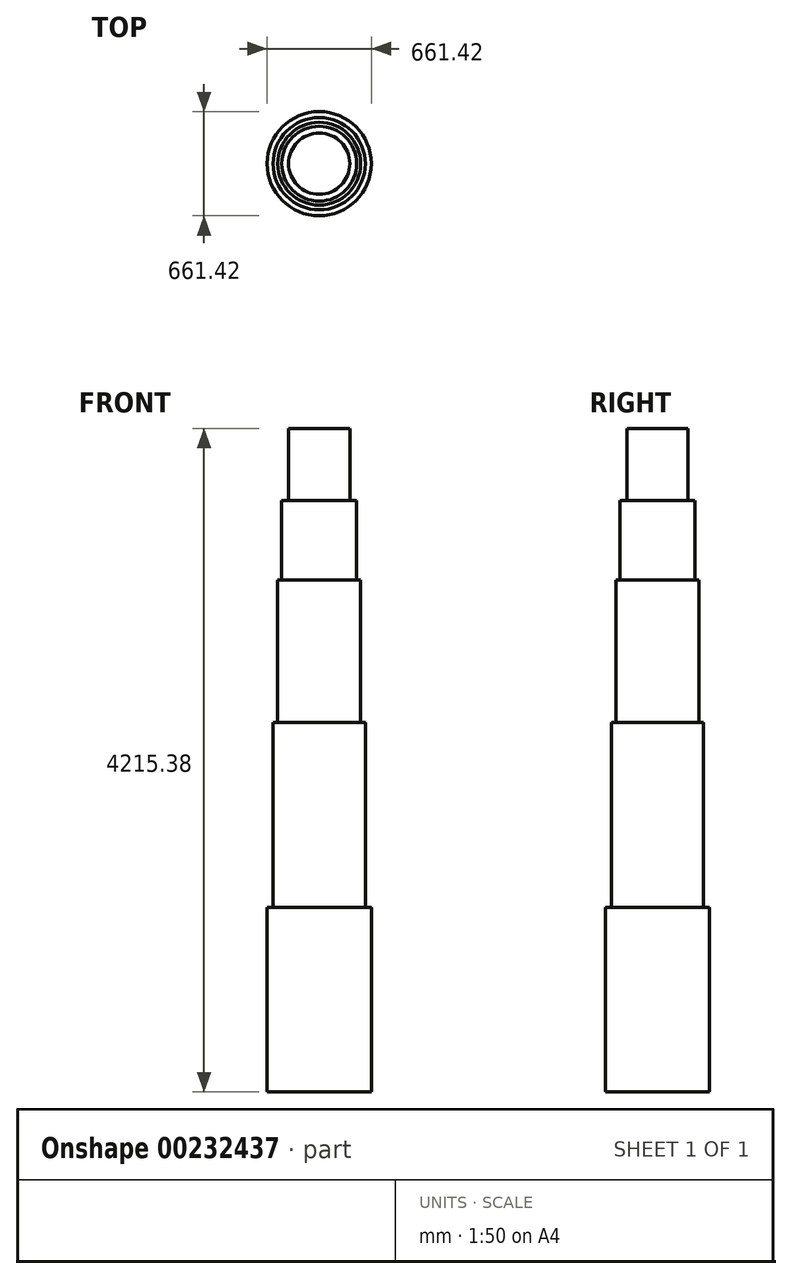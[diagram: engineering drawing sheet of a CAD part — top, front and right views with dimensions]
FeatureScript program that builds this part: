
annotation { "Feature Type Name" : "Feature", "Feature Type Description" : "" }
export const myFeature = defineFeature(function(context is Context, id is Id, definition is map)
    precondition{}
    {
        {
            var Q0;
            Q0=qCreatedBy(makeId("Top.planeOp"),FACE);
            var sketch = newSketch(context, id + "F0", { "sketchPlane" : qUnion([Q0])});
            skCircle(sketch, "E0", {"center": v(0, 0) * mm, "radius": 330.7 * mm});
            skSolve(sketch);
        }
        {
            var Q0;
            Q0 = qSketchRegion(id + "F0", true);
            extrude(context, id + "F1", {"entities" : qUnion([Q0]), "depth" : 1172.46 * mm});
        }
        {
            var Q0;
            Q0=makeQuery(id+"F1.opExtrude","CAP_FACE",FACE,{"disambiguationData":[OSD([sQuery(id+"F0.wireOp",EDGE,"E0")])],"isStart":false});
            var sketch = newSketch(context, id + "F2", { "sketchPlane" : qUnion([Q0])});
            skCircle(sketch, "E1", {"center": v(0, 0) * mm, "radius": 292.86 * mm});
            skSolve(sketch);
        }
        {
            var Q0;
            Q0 = qSketchRegion(id + "F2", true);
            extrude(context, id + "F3", {"entities" : qUnion([Q0]), "operationType" : NewBodyOperationType.ADD, "depth" : 1175 * mm});
        }
        {
            var Q0;
            Q0=makeQuery(id+"F3.opExtrude","CAP_FACE",FACE,{"disambiguationData":[OSD([sQuery(id+"F2.wireOp",EDGE,"E1")])],"isStart":false});
            var sketch = newSketch(context, id + "F4", { "sketchPlane" : qUnion([Q0])});
            skCircle(sketch, "E2", {"center": v(0, 0) * mm, "radius": 263.14 * mm});
            skSolve(sketch);
        }
        {
            var Q0;
            Q0 = qSketchRegion(id + "F4", true);
            extrude(context, id + "F5", {"entities" : qUnion([Q0]), "operationType" : NewBodyOperationType.ADD, "depth" : 905 * mm});
        }
        {
            var Q0;
            Q0=makeQuery(id+"F5.opExtrude","CAP_FACE",FACE,{"disambiguationData":[OSD([sQuery(id+"F4.wireOp",EDGE,"E2")])],"isStart":false});
            var sketch = newSketch(context, id + "F6", { "sketchPlane" : qUnion([Q0])});
            skCircle(sketch, "E3", {"center": v(0, 0) * mm, "radius": 237.74 * mm});
            skSolve(sketch);
        }
        {
            var Q0;
            Q0 = qSketchRegion(id + "F6", true);
            extrude(context, id + "F7", {"entities" : qUnion([Q0]), "operationType" : NewBodyOperationType.ADD, "depth" : 503.43 * mm});
        }
        {
            var Q0;
            Q0=makeQuery(id+"F7.opExtrude","CAP_FACE",FACE,{"disambiguationData":[OSD([sQuery(id+"F6.wireOp",EDGE,"E3")])],"isStart":false});
            var sketch = newSketch(context, id + "F8", { "sketchPlane" : qUnion([Q0])});
            skCircle(sketch, "E4", {"center": v(0, 0) * mm, "radius": 194.31 * mm});
            skSolve(sketch);
        }
        {
            var Q0;
            Q0 = qSketchRegion(id + "F8", true);
            extrude(context, id + "F9", {"entities" : qUnion([Q0]), "operationType" : NewBodyOperationType.ADD, "depth" : 459.5 * mm});
        }
    });
